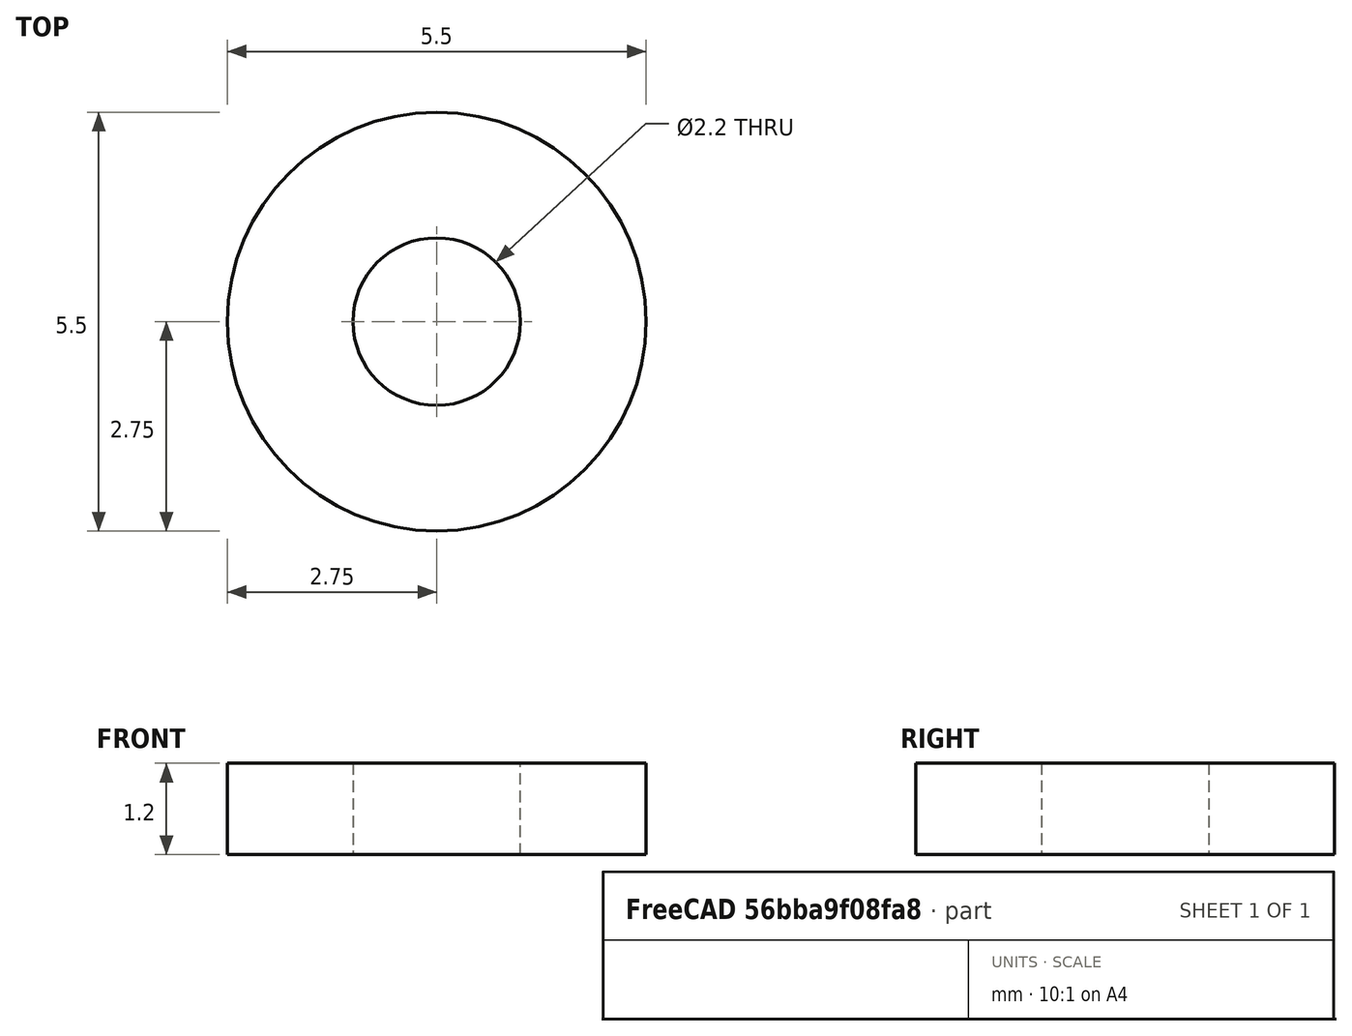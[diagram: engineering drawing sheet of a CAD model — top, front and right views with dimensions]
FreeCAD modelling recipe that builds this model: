
FCSTD DOCUMENT  (FreeCAD 0.18R13959 (Git))
Label: Washer_M2x1.2mm
License: CreativeCommons Attribution-NonCommercial-ShareAlike
LicenseURL: http://creativecommons.org/licenses/by-nc-sa/4.0/
objects: Sketcher::SketchObject×1, PartDesign::Pad×1, PartDesign::Body×1, Mesh::Feature×1
note: 4 computed .brp shape members not serialized (recipe doc carries the construction recipe); baked Part::Feature solids carry a one-line shape summary decoded from their .brp

FEATURE [Sketcher::SketchObject] Sketch
  MapMode = 5
  Support = -> [XY_Plane]
  sketch-geometry (2):
    g0: Circle CenterX=0 CenterY=0 CenterZ=0 NormalX=0 NormalY=0 NormalZ=1 AngleXU=0 Radius=2.75
    g1: Circle CenterX=0 CenterY=0 CenterZ=0 NormalX=0 NormalY=0 NormalZ=1 AngleXU=0 Radius=1.1
  constraints (4):
    c: Coincident(g0,g-1)
    c: Radius(g0) = 2.75
    c: Coincident(g1,g0)
    c: Radius(g1) = 1.1
FEATURE [PartDesign::Pad] Pad
  Length = 1.2
  Length2 = 100
  Profile = -> Sketch
  Type = 0
FEATURE [PartDesign::Body] Body
  Group = -> [Sketch,Pad]
  Origin = -> Origin
  Tip = -> Pad
FEATURE [Mesh::Feature] Mesh  label="Pad (Meshed)"
